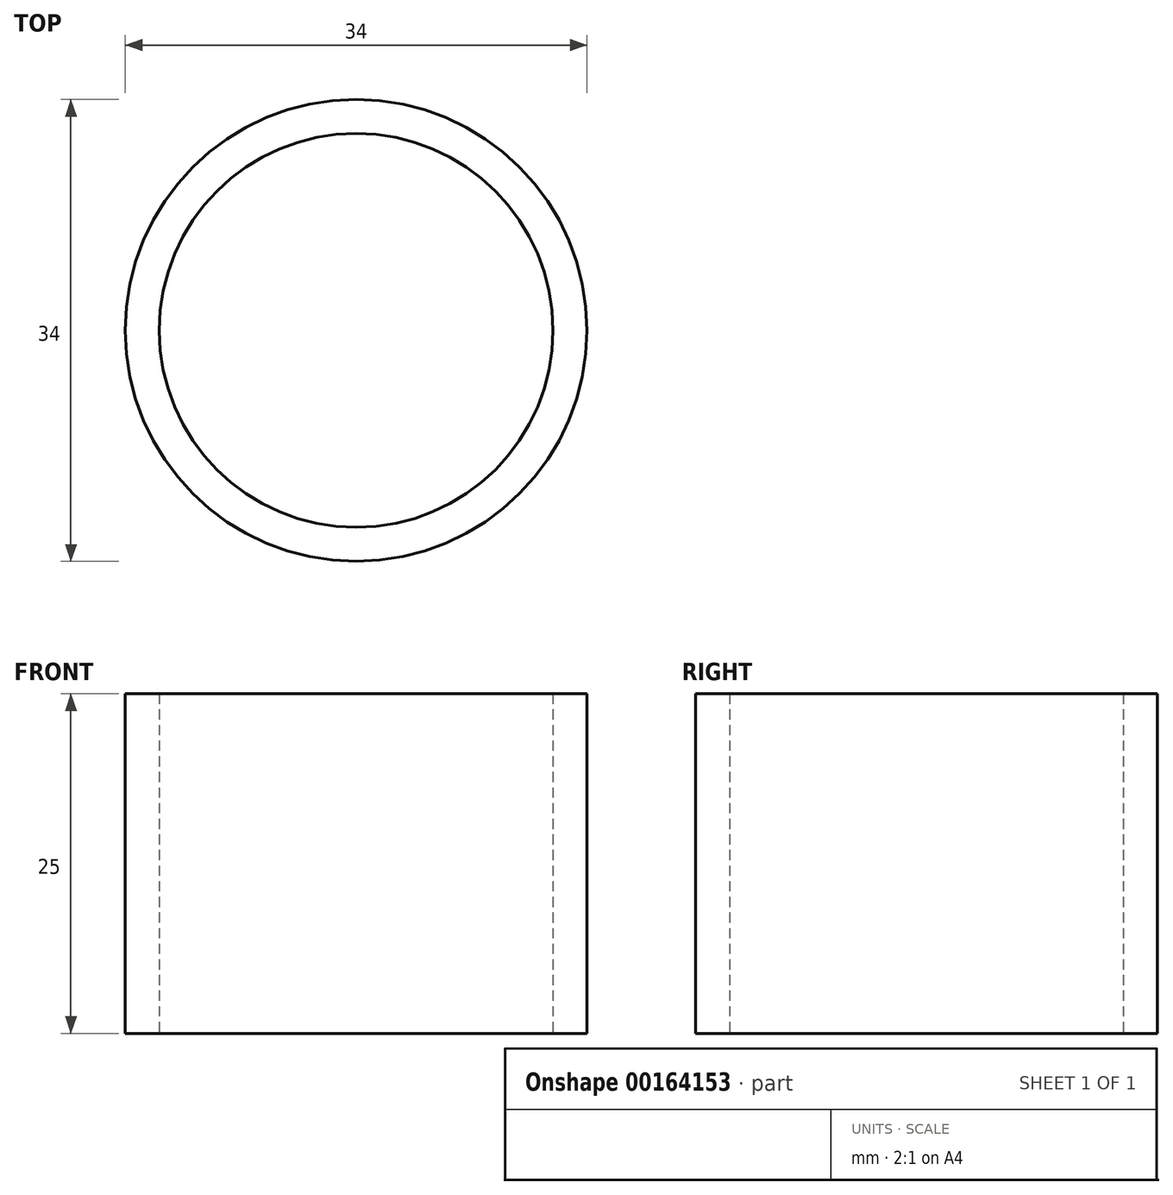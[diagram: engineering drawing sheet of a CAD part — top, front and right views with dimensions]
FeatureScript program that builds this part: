
annotation { "Feature Type Name" : "Feature", "Feature Type Description" : "" }
export const myFeature = defineFeature(function(context is Context, id is Id, definition is map)
    precondition{}
    {
        {
            var Q0;
            Q0=qCreatedBy(makeId("Top.planeOp"),FACE);
            var sketch = newSketch(context, id + "F0", { "sketchPlane" : qUnion([Q0])});
            skCircle(sketch, "E0", {"center": v(0, 0) * mm, "radius": 14.5 * mm});
            skCircle(sketch, "E1", {"center": v(0, 0) * mm, "radius": 17 * mm});
            skSolve(sketch);
        }
        {
            var Q0;
            Q0=makeQuery(id+"F0.imprint","IMPRINT",FACE,{"disambiguationData":[TD([[makeQuery(id+"F0.imprint","IMPRINT",EDGE,{"derivedFrom":sQuery(id+"F0.wireOp",EDGE,"E0")}),-1.0]])]});
            extrude(context, id + "F1", {"entities" : qUnion([Q0]), "depth" : 25 * mm});
        }
    });
